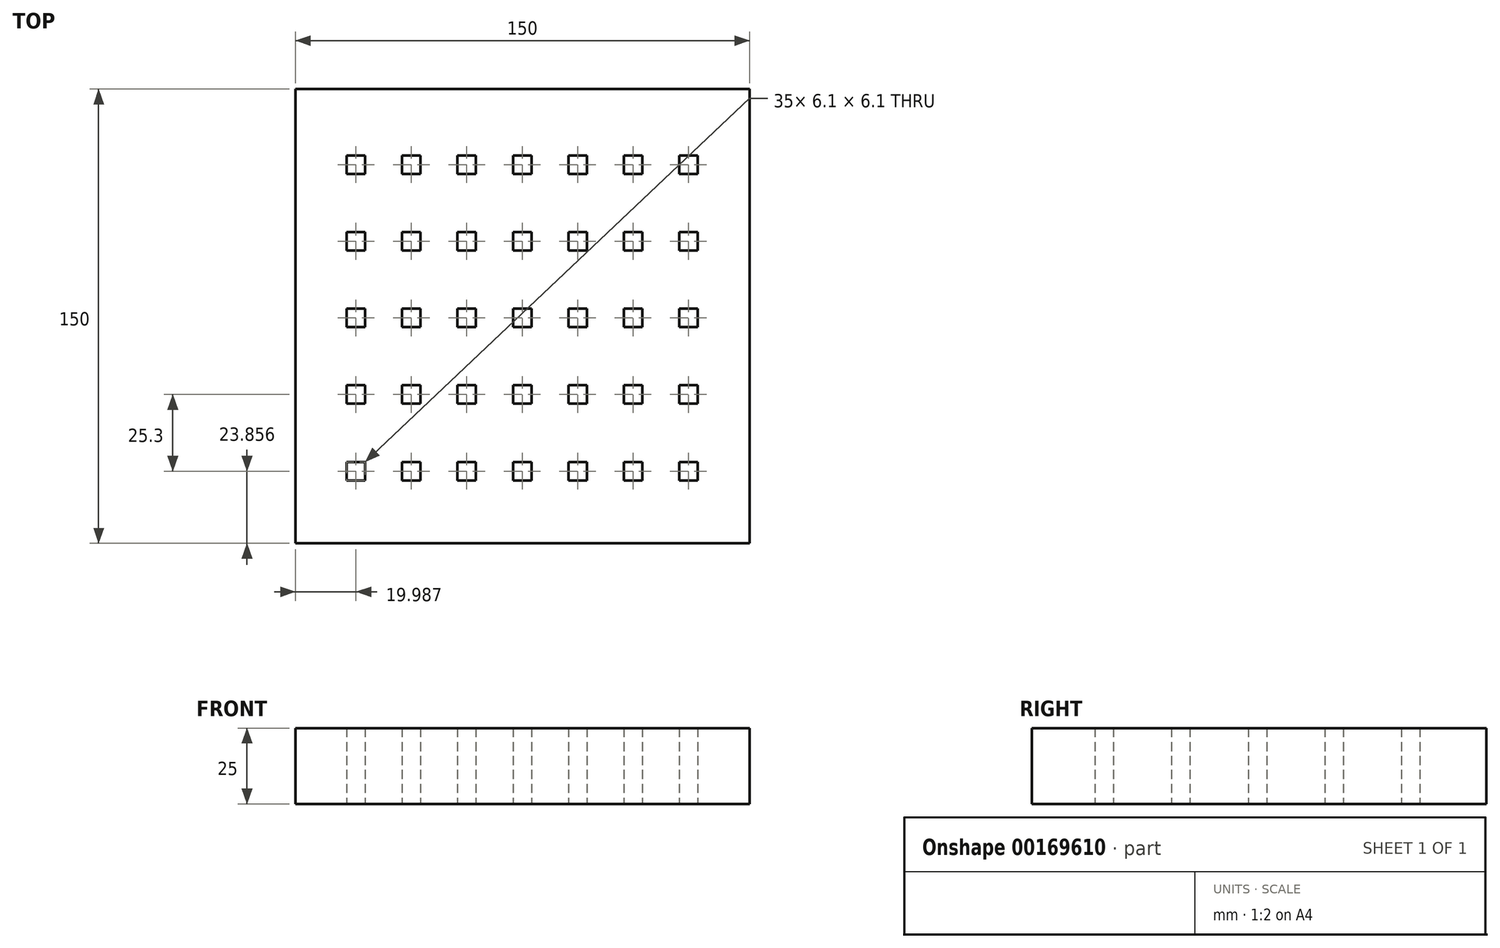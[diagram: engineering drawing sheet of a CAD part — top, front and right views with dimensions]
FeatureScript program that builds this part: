
annotation { "Feature Type Name" : "Feature", "Feature Type Description" : "" }
export const myFeature = defineFeature(function(context is Context, id is Id, definition is map)
    precondition{}
    {
        {
            var Q0;
            Q0=qCreatedBy(makeId("Top.planeOp"),FACE);
            var sketch = newSketch(context, id + "F0", { "sketchPlane" : qUnion([Q0])});
            skLineSegment(sketch, "E0.bottom", {"start": v(-93.3, 76.06) * mm, "end": v(56.7, 76.06) * mm});
            skLineSegment(sketch, "E0.top", {"start": v(-93.3, -73.94) * mm, "end": v(56.7, -73.94) * mm});
            skLineSegment(sketch, "E0.left", {"start": v(-93.3, 76.06) * mm, "end": v(-93.3, -73.94) * mm});
            skLineSegment(sketch, "E0.right", {"start": v(56.7, 76.06) * mm, "end": v(56.7, -73.94) * mm});
            skLineSegment(sketch, "E1.bottom", {"start": v(-76.37, 54.17) * mm, "end": v(-70.27, 54.17) * mm});
            skLineSegment(sketch, "E1.top", {"start": v(-76.37, 48.07) * mm, "end": v(-70.27, 48.07) * mm});
            skLineSegment(sketch, "E1.left", {"start": v(-76.37, 54.17) * mm, "end": v(-76.37, 48.07) * mm});
            skLineSegment(sketch, "E1.right", {"start": v(-70.27, 54.17) * mm, "end": v(-70.27, 48.07) * mm});
            skLineSegment(sketch, "E2", {"start": v(-93.3, 1.06) * mm, "end": v(56.7, 1.06) * mm, "construction": true});
            skLineSegment(sketch, "E3", {"start": v(-18.3, 76.06) * mm, "end": v(-18.3, -73.94) * mm, "construction": true});
            skLineSegment(sketch, "E4", {"start": v(-73.3, 76.06) * mm, "end": v(-73.3, 26.06) * mm, "construction": true});
            skLineSegment(sketch, "E5", {"start": v(-73.3, 26.06) * mm, "end": v(-73.3, -23.94) * mm, "construction": true});
            skLineSegment(sketch, "E6", {"start": v(-73.3, 1.06) * mm, "end": v(36.28, 1.06) * mm, "construction": true});
            skPoint(sketch, "E6.endSnap0", {"position": v(-73.3, 1.06) * mm});
            skLineSegment(sketch, "E7", {"start": v(-73.3, 51.06) * mm, "end": v(36.28, 51.06) * mm, "construction": true});
            skLineSegment(sketch, "E8", {"start": v(-73.3, 40.85) * mm, "end": v(-93.3, 40.85) * mm, "construction": true});
            skLineSegment(sketch, "E9", {"start": v(56.7, 37.2) * mm, "end": v(36.7, 37.2) * mm, "construction": true});
            skLineSegment(sketch, "E10", {"start": v(36.28, 76.06) * mm, "end": v(36.28, -73.94) * mm, "construction": true});
            skLineSegment(sketch, "E11.0.1.0", {"start": v(-76.37, 28.87) * mm, "end": v(-70.27, 28.87) * mm});
            skLineSegment(sketch, "E11.0.1.1", {"start": v(-76.37, 22.77) * mm, "end": v(-70.27, 22.77) * mm});
            skLineSegment(sketch, "E11.0.1.2", {"start": v(-76.37, 28.87) * mm, "end": v(-76.37, 22.77) * mm});
            skLineSegment(sketch, "E11.0.1.3", {"start": v(-70.27, 28.87) * mm, "end": v(-70.27, 22.77) * mm});
            skLineSegment(sketch, "E11.0.2.0", {"start": v(-76.37, 3.57) * mm, "end": v(-70.27, 3.57) * mm});
            skLineSegment(sketch, "E11.0.2.1", {"start": v(-76.37, -2.53) * mm, "end": v(-70.27, -2.53) * mm});
            skLineSegment(sketch, "E11.0.2.2", {"start": v(-76.37, 3.57) * mm, "end": v(-76.37, -2.53) * mm});
            skLineSegment(sketch, "E11.0.2.3", {"start": v(-70.27, 3.57) * mm, "end": v(-70.27, -2.53) * mm});
            skLineSegment(sketch, "E11.0.3.0", {"start": v(-76.37, -21.73) * mm, "end": v(-70.27, -21.73) * mm});
            skLineSegment(sketch, "E11.0.3.1", {"start": v(-76.37, -27.83) * mm, "end": v(-70.27, -27.83) * mm});
            skLineSegment(sketch, "E11.0.3.2", {"start": v(-76.37, -21.73) * mm, "end": v(-76.37, -27.83) * mm});
            skLineSegment(sketch, "E11.0.3.3", {"start": v(-70.27, -21.73) * mm, "end": v(-70.27, -27.83) * mm});
            skLineSegment(sketch, "E11.0.4.0", {"start": v(-76.37, -47.03) * mm, "end": v(-70.27, -47.03) * mm});
            skLineSegment(sketch, "E11.0.4.1", {"start": v(-76.37, -53.13) * mm, "end": v(-70.27, -53.13) * mm});
            skLineSegment(sketch, "E11.0.4.2", {"start": v(-76.37, -47.03) * mm, "end": v(-76.37, -53.13) * mm});
            skLineSegment(sketch, "E11.0.4.3", {"start": v(-70.27, -47.03) * mm, "end": v(-70.27, -53.13) * mm});
            skLineSegment(sketch, "E11.1.0.0", {"start": v(-58.07, 54.17) * mm, "end": v(-51.97, 54.17) * mm});
            skLineSegment(sketch, "E11.1.0.1", {"start": v(-58.07, 48.07) * mm, "end": v(-51.97, 48.07) * mm});
            skLineSegment(sketch, "E11.1.0.2", {"start": v(-58.07, 54.17) * mm, "end": v(-58.07, 48.07) * mm});
            skLineSegment(sketch, "E11.1.0.3", {"start": v(-51.97, 54.17) * mm, "end": v(-51.97, 48.07) * mm});
            skLineSegment(sketch, "E11.1.1.0", {"start": v(-58.07, 28.87) * mm, "end": v(-51.97, 28.87) * mm});
            skLineSegment(sketch, "E11.1.1.1", {"start": v(-58.07, 22.77) * mm, "end": v(-51.97, 22.77) * mm});
            skLineSegment(sketch, "E11.1.1.2", {"start": v(-58.07, 28.87) * mm, "end": v(-58.07, 22.77) * mm});
            skLineSegment(sketch, "E11.1.1.3", {"start": v(-51.97, 28.87) * mm, "end": v(-51.97, 22.77) * mm});
            skLineSegment(sketch, "E11.1.2.0", {"start": v(-58.07, 3.57) * mm, "end": v(-51.97, 3.57) * mm});
            skLineSegment(sketch, "E11.1.2.1", {"start": v(-58.07, -2.53) * mm, "end": v(-51.97, -2.53) * mm});
            skLineSegment(sketch, "E11.1.2.2", {"start": v(-58.07, 3.57) * mm, "end": v(-58.07, -2.53) * mm});
            skLineSegment(sketch, "E11.1.2.3", {"start": v(-51.97, 3.57) * mm, "end": v(-51.97, -2.53) * mm});
            skLineSegment(sketch, "E11.1.3.0", {"start": v(-58.07, -21.73) * mm, "end": v(-51.97, -21.73) * mm});
            skLineSegment(sketch, "E11.1.3.1", {"start": v(-58.07, -27.83) * mm, "end": v(-51.97, -27.83) * mm});
            skLineSegment(sketch, "E11.1.3.2", {"start": v(-58.07, -21.73) * mm, "end": v(-58.07, -27.83) * mm});
            skLineSegment(sketch, "E11.1.3.3", {"start": v(-51.97, -21.73) * mm, "end": v(-51.97, -27.83) * mm});
            skLineSegment(sketch, "E11.1.4.0", {"start": v(-58.07, -47.03) * mm, "end": v(-51.97, -47.03) * mm});
            skLineSegment(sketch, "E11.1.4.1", {"start": v(-58.07, -53.13) * mm, "end": v(-51.97, -53.13) * mm});
            skLineSegment(sketch, "E11.1.4.2", {"start": v(-58.07, -47.03) * mm, "end": v(-58.07, -53.13) * mm});
            skLineSegment(sketch, "E11.1.4.3", {"start": v(-51.97, -47.03) * mm, "end": v(-51.97, -53.13) * mm});
            skLineSegment(sketch, "E11.2.0.0", {"start": v(-39.77, 54.17) * mm, "end": v(-33.67, 54.17) * mm});
            skLineSegment(sketch, "E11.2.0.1", {"start": v(-39.77, 48.07) * mm, "end": v(-33.67, 48.07) * mm});
            skLineSegment(sketch, "E11.2.0.2", {"start": v(-39.77, 54.17) * mm, "end": v(-39.77, 48.07) * mm});
            skLineSegment(sketch, "E11.2.0.3", {"start": v(-33.67, 54.17) * mm, "end": v(-33.67, 48.07) * mm});
            skLineSegment(sketch, "E11.2.1.0", {"start": v(-39.77, 28.87) * mm, "end": v(-33.67, 28.87) * mm});
            skLineSegment(sketch, "E11.2.1.1", {"start": v(-39.77, 22.77) * mm, "end": v(-33.67, 22.77) * mm});
            skLineSegment(sketch, "E11.2.1.2", {"start": v(-39.77, 28.87) * mm, "end": v(-39.77, 22.77) * mm});
            skLineSegment(sketch, "E11.2.1.3", {"start": v(-33.67, 28.87) * mm, "end": v(-33.67, 22.77) * mm});
            skLineSegment(sketch, "E11.2.2.0", {"start": v(-39.77, 3.57) * mm, "end": v(-33.67, 3.57) * mm});
            skLineSegment(sketch, "E11.2.2.1", {"start": v(-39.77, -2.53) * mm, "end": v(-33.67, -2.53) * mm});
            skLineSegment(sketch, "E11.2.2.2", {"start": v(-39.77, 3.57) * mm, "end": v(-39.77, -2.53) * mm});
            skLineSegment(sketch, "E11.2.2.3", {"start": v(-33.67, 3.57) * mm, "end": v(-33.67, -2.53) * mm});
            skLineSegment(sketch, "E11.2.3.0", {"start": v(-39.77, -21.73) * mm, "end": v(-33.67, -21.73) * mm});
            skLineSegment(sketch, "E11.2.3.1", {"start": v(-39.77, -27.83) * mm, "end": v(-33.67, -27.83) * mm});
            skLineSegment(sketch, "E11.2.3.2", {"start": v(-39.77, -21.73) * mm, "end": v(-39.77, -27.83) * mm});
            skLineSegment(sketch, "E11.2.3.3", {"start": v(-33.67, -21.73) * mm, "end": v(-33.67, -27.83) * mm});
            skLineSegment(sketch, "E11.2.4.0", {"start": v(-39.77, -47.03) * mm, "end": v(-33.67, -47.03) * mm});
            skLineSegment(sketch, "E11.2.4.1", {"start": v(-39.77, -53.13) * mm, "end": v(-33.67, -53.13) * mm});
            skLineSegment(sketch, "E11.2.4.2", {"start": v(-39.77, -47.03) * mm, "end": v(-39.77, -53.13) * mm});
            skLineSegment(sketch, "E11.2.4.3", {"start": v(-33.67, -47.03) * mm, "end": v(-33.67, -53.13) * mm});
            skLineSegment(sketch, "E11.3.0.0", {"start": v(-21.47, 54.17) * mm, "end": v(-15.37, 54.17) * mm});
            skLineSegment(sketch, "E11.3.0.1", {"start": v(-21.47, 48.07) * mm, "end": v(-15.37, 48.07) * mm});
            skLineSegment(sketch, "E11.3.0.2", {"start": v(-21.47, 54.17) * mm, "end": v(-21.47, 48.07) * mm});
            skLineSegment(sketch, "E11.3.0.3", {"start": v(-15.37, 54.17) * mm, "end": v(-15.37, 48.07) * mm});
            skLineSegment(sketch, "E11.3.1.0", {"start": v(-21.47, 28.87) * mm, "end": v(-15.37, 28.87) * mm});
            skLineSegment(sketch, "E11.3.1.1", {"start": v(-21.47, 22.77) * mm, "end": v(-15.37, 22.77) * mm});
            skLineSegment(sketch, "E11.3.1.2", {"start": v(-21.47, 28.87) * mm, "end": v(-21.47, 22.77) * mm});
            skLineSegment(sketch, "E11.3.1.3", {"start": v(-15.37, 28.87) * mm, "end": v(-15.37, 22.77) * mm});
            skLineSegment(sketch, "E11.3.2.0", {"start": v(-21.47, 3.57) * mm, "end": v(-15.37, 3.57) * mm});
            skLineSegment(sketch, "E11.3.2.1", {"start": v(-21.47, -2.53) * mm, "end": v(-15.37, -2.53) * mm});
            skLineSegment(sketch, "E11.3.2.2", {"start": v(-21.47, 3.57) * mm, "end": v(-21.47, -2.53) * mm});
            skLineSegment(sketch, "E11.3.2.3", {"start": v(-15.37, 3.57) * mm, "end": v(-15.37, -2.53) * mm});
            skLineSegment(sketch, "E11.3.3.0", {"start": v(-21.47, -21.73) * mm, "end": v(-15.37, -21.73) * mm});
            skLineSegment(sketch, "E11.3.3.1", {"start": v(-21.47, -27.83) * mm, "end": v(-15.37, -27.83) * mm});
            skLineSegment(sketch, "E11.3.3.2", {"start": v(-21.47, -21.73) * mm, "end": v(-21.47, -27.83) * mm});
            skLineSegment(sketch, "E11.3.3.3", {"start": v(-15.37, -21.73) * mm, "end": v(-15.37, -27.83) * mm});
            skLineSegment(sketch, "E11.3.4.0", {"start": v(-21.47, -47.03) * mm, "end": v(-15.37, -47.03) * mm});
            skLineSegment(sketch, "E11.3.4.1", {"start": v(-21.47, -53.13) * mm, "end": v(-15.37, -53.13) * mm});
            skLineSegment(sketch, "E11.3.4.2", {"start": v(-21.47, -47.03) * mm, "end": v(-21.47, -53.13) * mm});
            skLineSegment(sketch, "E11.3.4.3", {"start": v(-15.37, -47.03) * mm, "end": v(-15.37, -53.13) * mm});
            skLineSegment(sketch, "E11.4.0.0", {"start": v(-3.17, 54.17) * mm, "end": v(2.93, 54.17) * mm});
            skLineSegment(sketch, "E11.4.0.1", {"start": v(-3.17, 48.07) * mm, "end": v(2.93, 48.07) * mm});
            skLineSegment(sketch, "E11.4.0.2", {"start": v(-3.17, 54.17) * mm, "end": v(-3.17, 48.07) * mm});
            skLineSegment(sketch, "E11.4.0.3", {"start": v(2.93, 54.17) * mm, "end": v(2.93, 48.07) * mm});
            skLineSegment(sketch, "E11.4.1.0", {"start": v(-3.17, 28.87) * mm, "end": v(2.93, 28.87) * mm});
            skLineSegment(sketch, "E11.4.1.1", {"start": v(-3.17, 22.77) * mm, "end": v(2.93, 22.77) * mm});
            skLineSegment(sketch, "E11.4.1.2", {"start": v(-3.17, 28.87) * mm, "end": v(-3.17, 22.77) * mm});
            skLineSegment(sketch, "E11.4.1.3", {"start": v(2.93, 28.87) * mm, "end": v(2.93, 22.77) * mm});
            skLineSegment(sketch, "E11.4.2.0", {"start": v(-3.17, 3.57) * mm, "end": v(2.93, 3.57) * mm});
            skLineSegment(sketch, "E11.4.2.1", {"start": v(-3.17, -2.53) * mm, "end": v(2.93, -2.53) * mm});
            skLineSegment(sketch, "E11.4.2.2", {"start": v(-3.17, 3.57) * mm, "end": v(-3.17, -2.53) * mm});
            skLineSegment(sketch, "E11.4.2.3", {"start": v(2.93, 3.57) * mm, "end": v(2.93, -2.53) * mm});
            skLineSegment(sketch, "E11.4.3.0", {"start": v(-3.17, -21.73) * mm, "end": v(2.93, -21.73) * mm});
            skLineSegment(sketch, "E11.4.3.1", {"start": v(-3.17, -27.83) * mm, "end": v(2.93, -27.83) * mm});
            skLineSegment(sketch, "E11.4.3.2", {"start": v(-3.17, -21.73) * mm, "end": v(-3.17, -27.83) * mm});
            skLineSegment(sketch, "E11.4.3.3", {"start": v(2.93, -21.73) * mm, "end": v(2.93, -27.83) * mm});
            skLineSegment(sketch, "E11.4.4.0", {"start": v(-3.17, -47.03) * mm, "end": v(2.93, -47.03) * mm});
            skLineSegment(sketch, "E11.4.4.1", {"start": v(-3.17, -53.13) * mm, "end": v(2.93, -53.13) * mm});
            skLineSegment(sketch, "E11.4.4.2", {"start": v(-3.17, -47.03) * mm, "end": v(-3.17, -53.13) * mm});
            skLineSegment(sketch, "E11.4.4.3", {"start": v(2.93, -47.03) * mm, "end": v(2.93, -53.13) * mm});
            skLineSegment(sketch, "E11.5.0.0", {"start": v(15.13, 54.17) * mm, "end": v(21.23, 54.17) * mm});
            skLineSegment(sketch, "E11.5.0.1", {"start": v(15.13, 48.07) * mm, "end": v(21.23, 48.07) * mm});
            skLineSegment(sketch, "E11.5.0.2", {"start": v(15.13, 54.17) * mm, "end": v(15.13, 48.07) * mm});
            skLineSegment(sketch, "E11.5.0.3", {"start": v(21.23, 54.17) * mm, "end": v(21.23, 48.07) * mm});
            skLineSegment(sketch, "E11.5.1.0", {"start": v(15.13, 28.87) * mm, "end": v(21.23, 28.87) * mm});
            skLineSegment(sketch, "E11.5.1.1", {"start": v(15.13, 22.77) * mm, "end": v(21.23, 22.77) * mm});
            skLineSegment(sketch, "E11.5.1.2", {"start": v(15.13, 28.87) * mm, "end": v(15.13, 22.77) * mm});
            skLineSegment(sketch, "E11.5.1.3", {"start": v(21.23, 28.87) * mm, "end": v(21.23, 22.77) * mm});
            skLineSegment(sketch, "E11.5.2.0", {"start": v(15.13, 3.57) * mm, "end": v(21.23, 3.57) * mm});
            skLineSegment(sketch, "E11.5.2.1", {"start": v(15.13, -2.53) * mm, "end": v(21.23, -2.53) * mm});
            skLineSegment(sketch, "E11.5.2.2", {"start": v(15.13, 3.57) * mm, "end": v(15.13, -2.53) * mm});
            skLineSegment(sketch, "E11.5.2.3", {"start": v(21.23, 3.57) * mm, "end": v(21.23, -2.53) * mm});
            skLineSegment(sketch, "E11.5.3.0", {"start": v(15.13, -21.73) * mm, "end": v(21.23, -21.73) * mm});
            skLineSegment(sketch, "E11.5.3.1", {"start": v(15.13, -27.83) * mm, "end": v(21.23, -27.83) * mm});
            skLineSegment(sketch, "E11.5.3.2", {"start": v(15.13, -21.73) * mm, "end": v(15.13, -27.83) * mm});
            skLineSegment(sketch, "E11.5.3.3", {"start": v(21.23, -21.73) * mm, "end": v(21.23, -27.83) * mm});
            skLineSegment(sketch, "E11.5.4.0", {"start": v(15.13, -47.03) * mm, "end": v(21.23, -47.03) * mm});
            skLineSegment(sketch, "E11.5.4.1", {"start": v(15.13, -53.13) * mm, "end": v(21.23, -53.13) * mm});
            skLineSegment(sketch, "E11.5.4.2", {"start": v(15.13, -47.03) * mm, "end": v(15.13, -53.13) * mm});
            skLineSegment(sketch, "E11.5.4.3", {"start": v(21.23, -47.03) * mm, "end": v(21.23, -53.13) * mm});
            skLineSegment(sketch, "E11.6.0.0", {"start": v(33.43, 54.17) * mm, "end": v(39.53, 54.17) * mm});
            skLineSegment(sketch, "E11.6.0.1", {"start": v(33.43, 48.07) * mm, "end": v(39.53, 48.07) * mm});
            skLineSegment(sketch, "E11.6.0.2", {"start": v(33.43, 54.17) * mm, "end": v(33.43, 48.07) * mm});
            skLineSegment(sketch, "E11.6.0.3", {"start": v(39.53, 54.17) * mm, "end": v(39.53, 48.07) * mm});
            skLineSegment(sketch, "E11.6.1.0", {"start": v(33.43, 28.87) * mm, "end": v(39.53, 28.87) * mm});
            skLineSegment(sketch, "E11.6.1.1", {"start": v(33.43, 22.77) * mm, "end": v(39.53, 22.77) * mm});
            skLineSegment(sketch, "E11.6.1.2", {"start": v(33.43, 28.87) * mm, "end": v(33.43, 22.77) * mm});
            skLineSegment(sketch, "E11.6.1.3", {"start": v(39.53, 28.87) * mm, "end": v(39.53, 22.77) * mm});
            skLineSegment(sketch, "E11.6.2.0", {"start": v(33.43, 3.57) * mm, "end": v(39.53, 3.57) * mm});
            skLineSegment(sketch, "E11.6.2.1", {"start": v(33.43, -2.53) * mm, "end": v(39.53, -2.53) * mm});
            skLineSegment(sketch, "E11.6.2.2", {"start": v(33.43, 3.57) * mm, "end": v(33.43, -2.53) * mm});
            skLineSegment(sketch, "E11.6.2.3", {"start": v(39.53, 3.57) * mm, "end": v(39.53, -2.53) * mm});
            skLineSegment(sketch, "E11.6.3.0", {"start": v(33.43, -21.73) * mm, "end": v(39.53, -21.73) * mm});
            skLineSegment(sketch, "E11.6.3.1", {"start": v(33.43, -27.83) * mm, "end": v(39.53, -27.83) * mm});
            skLineSegment(sketch, "E11.6.3.2", {"start": v(33.43, -21.73) * mm, "end": v(33.43, -27.83) * mm});
            skLineSegment(sketch, "E11.6.3.3", {"start": v(39.53, -21.73) * mm, "end": v(39.53, -27.83) * mm});
            skLineSegment(sketch, "E11.6.4.0", {"start": v(33.43, -47.03) * mm, "end": v(39.53, -47.03) * mm});
            skLineSegment(sketch, "E11.6.4.1", {"start": v(33.43, -53.13) * mm, "end": v(39.53, -53.13) * mm});
            skLineSegment(sketch, "E11.6.4.2", {"start": v(33.43, -47.03) * mm, "end": v(33.43, -53.13) * mm});
            skLineSegment(sketch, "E11.6.4.3", {"start": v(39.53, -47.03) * mm, "end": v(39.53, -53.13) * mm});
            skLineSegment(sketch, "E11.direction1", {"start": v(-76.37, 48.07) * mm, "end": v(-58.07, 48.07) * mm, "construction": true});
            skLineSegment(sketch, "E11.direction2", {"start": v(-76.37, 48.07) * mm, "end": v(-76.37, 22.77) * mm, "construction": true});
            skSolve(sketch);
        }
        {
            var Q0;
            Q0 = qSketchRegion(id + "F0", true);
            extrude(context, id + "F1", {"entities" : qUnion([Q0]), "depth" : 25 * mm, "offsetDistance" : 25 * mm});
        }
    });
